# Revit family: Basin-Multi_Station-Sloan-SloanStone-ELWF-Series
name_source: partatom
category: Plumbing Fixtures
revit_build: Autodesk Revit 2014 (Build: 20130308_1515(x64)
units: mm (PartAtom-declared; Revit-internal decimal feet)

## types (3) — shared parameters
ADA Compliant = Yes
Assembly Code = D2010300
Basin Shape = Rectangular
CW Connection = Yes
CW Connection 1 = 1/2'' CW Inlet 1
CW Connection 2 = 1/2'' CW Inlet 2
CWFU = 1.5
Cold Water Connection Diameter = 1/2"
Cold Water Connection Height = 15"
Cold Water Connection Width = 2"
Default Elevation = 0"
Description = Two station solid surface waterfall lavatory system equipped with Sloan sensor activated faucets.
Description Waste 1 = 1 1/2'' Waste Connection Outlet
Description Waste 2 = 1 1/2'' Waste Connection Outlet
Diameter Faucet 1 = 1/2"
Diameter Faucet 2 = 1/2"
Diameter Waste 1 = 1 1/2"
Diameter Waste 2 = 1 1/2"
Faucet 1 = Yes
Faucet 2 = Yes
Finish = SloanStone-Sloan-WH-White
HW Connection = Yes
HW Connection 1 = 1/2'' HW Inlet 1
HW Connection 2 = 1/2'' HW Inlet 2
HWFU = 1.5
Height = 30"
Hot Water Connection Diameter = 1"
Hot Water Connection Height = 15"
Hot Water Connection Width = 2"
IAPMO Compliance = UPC
Installation Type = Wall Mounted
Manufacturer = Sloan
Material = SloanStone-Sloan-WH-White
Price = Prices may vary. Please consult Manufacturer Representative for most up-to-date price list.
Product Documentation Link = https://specifications.sloan.com
URL = https://www.sloan.com
Vent Connection = No
WFU = 2
Warranty Information = 3 Year (Limited)
Waste Connection = Yes
Waste Connection Diameter = 1 1/2"
Waste Connection Height = 13"
Width = 22"

## per-type parameters (varying)
| type | CW Connection 3 | CW Connection 4 | Description Waste 3 | Description Waste 4 | Diameter Faucet 3 | Diameter Faucet 4 | Diameter Waste 3 | Diameter Waste 4 | Faucet 3 | Faucet 4 | HW Connection 3 | HW Connection 4 | Length | Model | Waste 1 Location |
| ELWF-82000 |  |  |  |  | 0" | 0" | 0" | 0" | No | No |  |  | 60" | ELWF-82000 | 30" |
| ELWF-83000 | 1/2'' CW Inlet 3 |  | 1 1/2'' Waste Connection Outlet |  | 1/2" | 0" | 1 1/2" | 0" | Yes | No | 1/2'' HW Inlet 3 |  | 90" | ELWF-83000 | 45" |
| ELWF-84000 | 1/2'' CW Inlet 3 | 1/2'' CW Inlet 4 | 1 1/2'' Waste Connection Outlet | 1 1/2'' Waste Connection Outlet | 1/2" | 1/2" | 1 1/2" | 1 1/2" | Yes | Yes | 1/2'' HW Inlet 3 | 1/2'' HW Inlet 4 | 120" | ELWF-83000 | 39 1/2" |

## geometry (parser evidence)
native form markers: Sweep x1
no freeform markers — native parametric forms only
